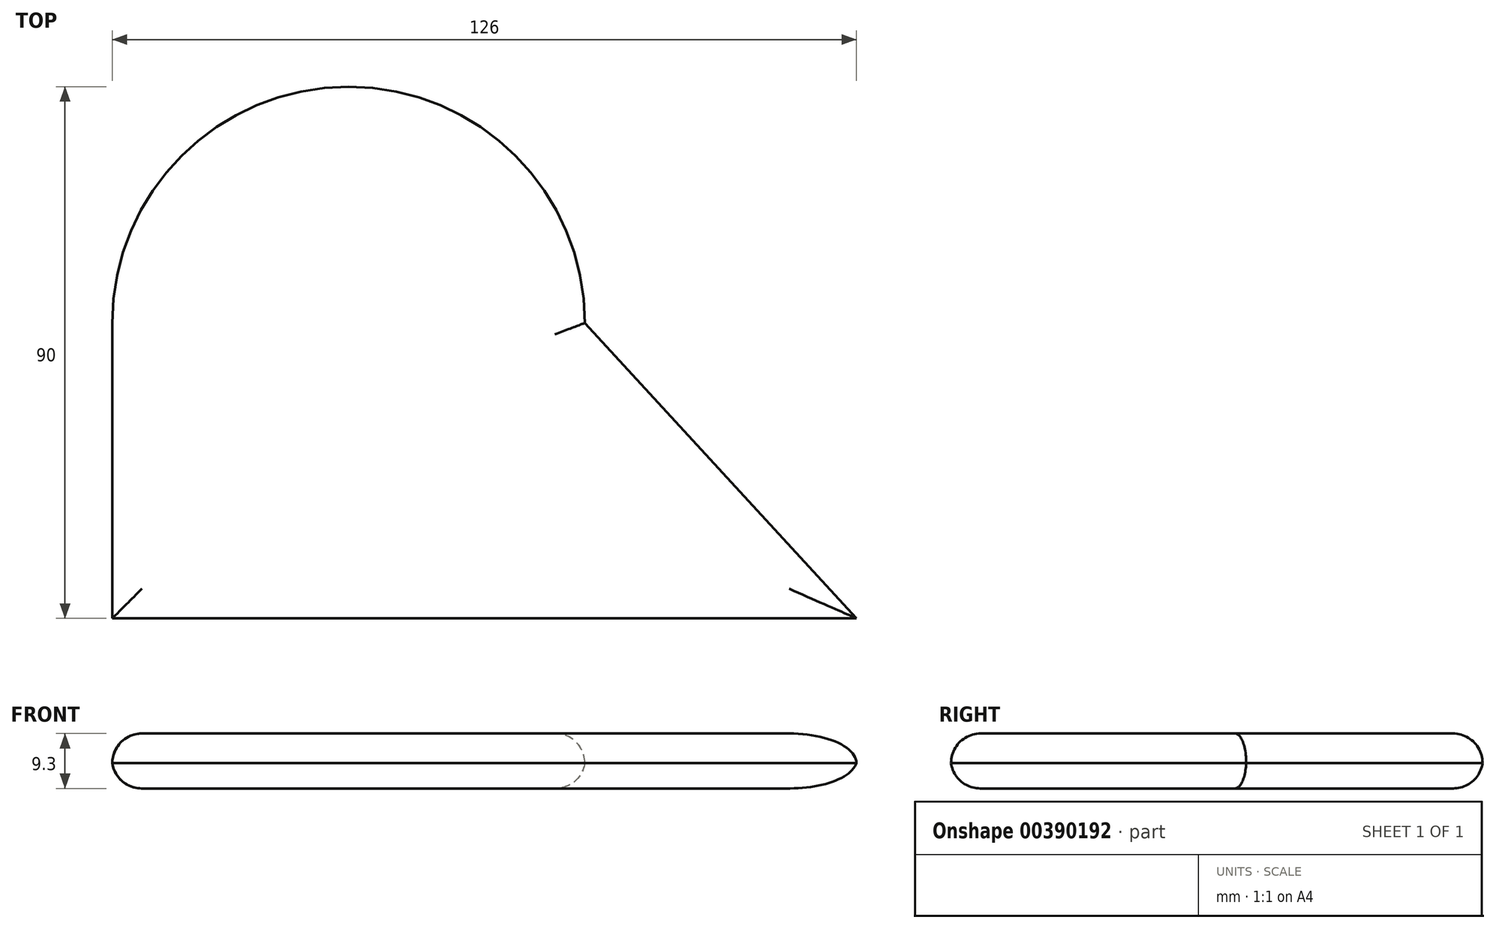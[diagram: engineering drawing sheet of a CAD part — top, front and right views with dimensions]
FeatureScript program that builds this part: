
annotation { "Feature Type Name" : "Feature", "Feature Type Description" : "" }
export const myFeature = defineFeature(function(context is Context, id is Id, definition is map)
    precondition{}
    {
        {
            var Q0;
            Q0=qCreatedBy(makeId("Top.planeOp"),FACE);
            var sketch = newSketch(context, id + "F0", { "sketchPlane" : qUnion([Q0])});
            skLineSegment(sketch, "E0.bottom", {"start": v(-67.89, 31.39) * mm, "end": v(12.11, 31.39) * mm});
            skLineSegment(sketch, "E0.top", {"start": v(-67.89, -18.61) * mm, "end": v(12.11, -18.61) * mm});
            skLineSegment(sketch, "E0.left", {"start": v(-67.89, 31.39) * mm, "end": v(-67.89, -18.61) * mm});
            skLineSegment(sketch, "E0.right", {"start": v(12.11, 31.39) * mm, "end": v(12.11, -18.61) * mm});
            skArc(sketch, "E1", {"start": v(12.11, 31.39) * mm, "mid": v(-27.89, 71.39) * mm, "end": v(-67.89, 31.39) * mm});
            skLineSegment(sketch, "E2", {"start": v(12.11, -18.61) * mm, "end": v(58.11, -18.61) * mm});
            skLineSegment(sketch, "E3", {"start": v(12.11, 31.39) * mm, "end": v(58.11, -18.61) * mm});
            skSolve(sketch);
        }
        {
            var Q0;
            Q0 = qSketchRegion(id + "F0", true);
            extrude(context, id + "F1", {"entities" : qUnion([Q0]), "depth" : 9.3 * mm});
        }
        {
            var Q0;
            Q0=makeQuery(id+"F1.opExtrude","CAP_FACE",FACE,{"disambiguationData":[OSD([sQuery(id+"F0.wireOp",EDGE,"E0.top"),sQuery(id+"F0.wireOp",EDGE,"E0.left"),sQuery(id+"F0.wireOp",EDGE,"E1"),sQuery(id+"F0.wireOp",EDGE,"E2"),sQuery(id+"F0.wireOp",EDGE,"E3")])],"isStart":false});
            fillet(context, id + "F2", {"entities" : qUnion([Q0]), "radius" : 5 * mm, "tangentPropagation" : true, "allowEdgeOverflow" : false});
        }
        {
            var Q0;
            Q0=makeQuery(id+"F1.opExtrude","CAP_FACE",FACE,{"disambiguationData":[OSD([sQuery(id+"F0.wireOp",EDGE,"E0.top"),sQuery(id+"F0.wireOp",EDGE,"E0.left"),sQuery(id+"F0.wireOp",EDGE,"E1"),sQuery(id+"F0.wireOp",EDGE,"E2"),sQuery(id+"F0.wireOp",EDGE,"E3")])],"isStart":true});
            fillet(context, id + "F3", {"entities" : qUnion([Q0]), "radius" : 5 * mm, "tangentPropagation" : true, "allowEdgeOverflow" : false});
        }
    });
